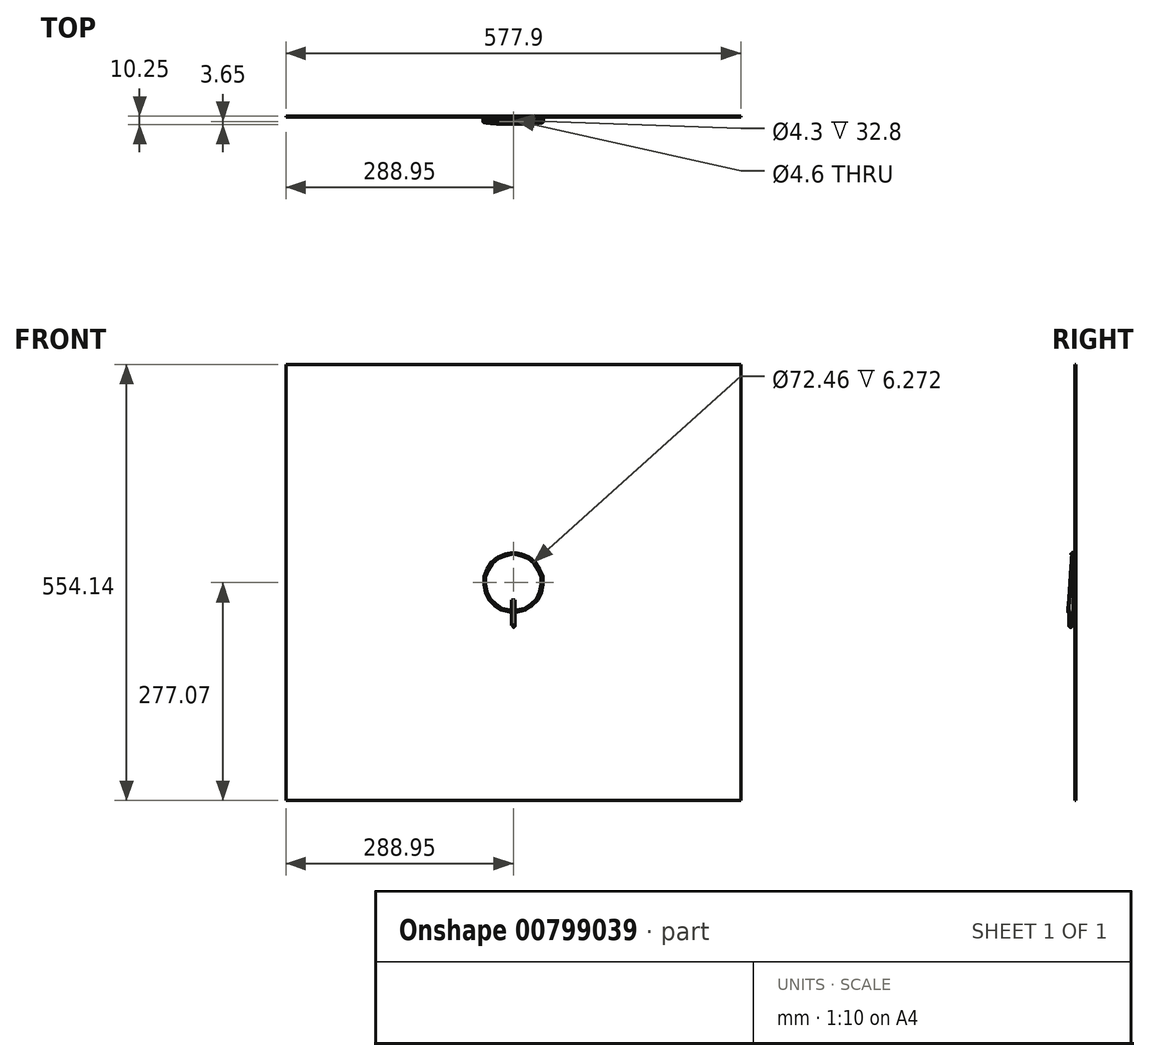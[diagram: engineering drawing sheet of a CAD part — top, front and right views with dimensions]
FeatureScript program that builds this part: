
annotation { "Feature Type Name" : "Feature", "Feature Type Description" : "" }
export const myFeature = defineFeature(function(context is Context, id is Id, definition is map)
    precondition{}
    {
        {
            var Q0;
            Q0=qCreatedBy(makeId("Front.planeOp"),FACE);
            var sketch = newSketch(context, id + "F0", { "sketchPlane" : qUnion([Q0])});
            skCircle(sketch, "E0", {"center": v(0, 0) * mm, "radius": 38.46 * mm});
            skCircle(sketch, "E1", {"center": v(0, 0) * mm, "radius": 36.23 * mm});
            skSolve(sketch);
        }
        {
            var Q0;
            Q0=makeQuery(id+"F0.imprint","IMPRINT",FACE,{"disambiguationData":[TD([[makeQuery(id+"F0.imprint","IMPRINT",EDGE,{"derivedFrom":sQuery(id+"F0.wireOp",EDGE,"E0")}),1.0]])]});
            extrude(context, id + "F1", {"entities" : qUnion([Q0]), "depth" : 8.4 * mm, "offsetDistance" : 25 * mm});
        }
        {
            var Q0;
            Q0=qCreatedBy(makeId("Right.planeOp"),FACE);
            var sketch = newSketch(context, id + "F2", { "sketchPlane" : qUnion([Q0])});
            skLineSegment(sketch, "E2", {"start": v(-21.96, 45.14) * mm, "end": v(-4.24, 45.14) * mm});
            skLineSegment(sketch, "E3", {"start": v(-4.24, 45.14) * mm, "end": v(-2, 39.27) * mm});
            skLineSegment(sketch, "E4", {"start": v(-2, 39.27) * mm, "end": v(-8, -48.33) * mm});
            skLineSegment(sketch, "E5", {"start": v(-8, -48.33) * mm, "end": v(-24.72, -40.34) * mm});
            skLineSegment(sketch, "E6", {"start": v(-24.72, -40.34) * mm, "end": v(-21.96, 45.14) * mm});
            skSolve(sketch);
        }
        {
            var Q0;
            Q0 = qSketchRegion(id + "F2", true);
            extrude(context, id + "F3", {"entities" : qUnion([Q0]), "operationType" : NewBodyOperationType.REMOVE, "endBound" : BoundingType.SYMMETRIC, "oppositeDirection" : true, "depth" : 106 * mm, "offsetDistance" : 25 * mm});
        }
        {
            var Q0;
            Q0=makeQuery(id+"F3.boolean.opBoolean","INTERSECT",EDGE,{"derivedFrom":[makeQuery(id+"F1.opExtrude","SWEPT_FACE",FACE,{"disambiguationData":[OSD([sQuery(id+"F0.wireOp",EDGE,"E1")])]}),makeQuery(id+"F3.opExtrude","SWEPT_FACE",FACE,{"disambiguationData":[OSD([sQuery(id+"F2.wireOp",EDGE,"E4")])]})]});
            var Q1;
            Q1=makeQuery(id+"F3.boolean.opBoolean","INTERSECT",EDGE,{"derivedFrom":[makeQuery(id+"F1.opExtrude","SWEPT_FACE",FACE,{"disambiguationData":[OSD([sQuery(id+"F0.wireOp",EDGE,"E0")])]}),makeQuery(id+"F3.opExtrude","SWEPT_FACE",FACE,{"disambiguationData":[OSD([sQuery(id+"F2.wireOp",EDGE,"E4")])]})]});
            fillet(context, id + "F4", {"entities" : qUnion([Q0, Q1]), "radius" : 1 * mm, "tangentPropagation" : true, "allowEdgeOverflow" : false});
        }
        {
            var Q0;
            Q0=qCreatedBy(makeId("Top.planeOp"),FACE);
            var sketch = newSketch(context, id + "F5", { "sketchPlane" : qUnion([Q0])});
            skCircle(sketch, "E7", {"center": v(0, -3.6) * mm, "radius": 2.3 * mm});
            skSolve(sketch);
        }
        {
            var Q0;
            Q0=qCreatedBy(makeId("Top.planeOp"),FACE);
            cPlane(context, id + "F6", {"entities" : qUnion([Q0]), "cplaneType" : CPlaneType.OFFSET, "offset" : 22 * mm, "oppositeDirection" : true, "width" : 150 * mm, "height" : 150 * mm});
        }
        {
            var Q0;
            Q0=qCreatedBy(id+"F6.planeOp",FACE);
            var sketch = newSketch(context, id + "F7", { "sketchPlane" : qUnion([Q0])});
            skCircle(sketch, "E8", {"center": v(0, -3.6) * mm, "radius": 2.25 * mm});
            skSolve(sketch);
        }
        {
            var Q0;
            Q0=makeQuery(id+"F5.imprint","IMPRINT",FACE,{"disambiguationData":[TD([[makeQuery(id+"F5.imprint","IMPRINT",EDGE,{"derivedFrom":sQuery(id+"F5.wireOp",EDGE,"E7")}),1.0]])]});
            extrude(context, id + "F8", {"entities" : qUnion([Q0]), "operationType" : NewBodyOperationType.REMOVE, "oppositeDirection" : true, "depth" : 45.9 * mm, "offsetDistance" : 25 * mm});
        }
        {
            var Q0;
            Q0=makeQuery(id+"F8.boolean.opBoolean","INTERSECT",EDGE,{"derivedFrom":[makeQuery(id+"F1.opExtrude","SWEPT_FACE",FACE,{"disambiguationData":[OSD([sQuery(id+"F0.wireOp",EDGE,"E1")])]}),makeQuery(id+"F8.opExtrude","SWEPT_FACE",FACE,{"disambiguationData":[OSD([sQuery(id+"F5.wireOp",EDGE,"E7")])]})]});
            var Q1;
            Q1=makeQuery(id+"F8.boolean.opBoolean","INTERSECT",EDGE,{"derivedFrom":[makeQuery(id+"F1.opExtrude","SWEPT_FACE",FACE,{"disambiguationData":[OSD([sQuery(id+"F0.wireOp",EDGE,"E0")])]}),makeQuery(id+"F8.opExtrude","SWEPT_FACE",FACE,{"disambiguationData":[OSD([sQuery(id+"F5.wireOp",EDGE,"E7")])]})]});
            fillet(context, id + "F9", {"entities" : qUnion([Q0, Q1]), "radius" : 0.3 * mm, "tangentPropagation" : true, "allowEdgeOverflow" : false});
        }
        {
            var Q0;
            Q0 = qSketchRegion(id + "F7", true);
            extrude(context, id + "F10", {"entities" : qUnion([Q0]), "operationType" : NewBodyOperationType.ADD, "oppositeDirection" : true, "depth" : 35 * mm, "offsetDistance" : 25 * mm});
        }
        {
            var Q0;
            Q0=makeQuery(id+"F10.opExtrude","CAP_EDGE",EDGE,{"disambiguationData":[OSD([sQuery(id+"F7.wireOp",EDGE,"E8")])],"isStart":false});
            fillet(context, id + "F11", {"entities" : qUnion([Q0]), "radius" : 2.2 * mm, "tangentPropagation" : true, "allowEdgeOverflow" : false});
        }
        {
            var Q0;
            Q0=makeQuery(id+"F10.opExtrude","CAP_FACE",FACE,{"disambiguationData":[OSD([sQuery(id+"F7.wireOp",EDGE,"E8")])],"isStart":true});
            shell(context, id + "F12", {"entities" : qUnion([Q0]), "thickness" : 0.1 * mm});
        }
        {
            var Q0;
            Q0=qCreatedBy(makeId("Right.planeOp"),FACE);
            var sketch = newSketch(context, id + "F13", { "sketchPlane" : qUnion([Q0])});
            skLineSegment(sketch, "E9", {"start": v(2, 35.83) * mm, "end": v(-1.89, 35.83) * mm});
            skLineSegment(sketch, "E10", {"start": v(-1.89, 35.83) * mm, "end": v(-3.62, 36.57) * mm});
            skSolve(sketch);
        }
        {
            var Q0;
            Q0=qCreatedBy(makeId("Front.planeOp"),FACE);
            cPlane(context, id + "F14", {"entities" : qUnion([Q0]), "cplaneType" : CPlaneType.OFFSET, "offset" : 2 * mm, "oppositeDirection" : true, "width" : 150 * mm, "height" : 150 * mm});
        }
        {
            var Q0;
            Q0=qCreatedBy(id+"F14.planeOp",FACE);
            var sketch = newSketch(context, id + "F15", { "sketchPlane" : qUnion([Q0])});
            skCircle(sketch, "E11", {"center": v(0, 35.84) * mm, "radius": 0.35 * mm});
            skSolve(sketch);
        }
        {
            var Q0;
            Q0=makeQuery(id+"F15.imprint","IMPRINT",FACE,{"disambiguationData":[TD([[makeQuery(id+"F15.imprint","IMPRINT",EDGE,{"derivedFrom":sQuery(id+"F15.wireOp",EDGE,"E11")}),1.0]])]});
            var Q1;
            Q1=sQuery(id+"F13.wireOp",EDGE,"E9");
            var Q2;
            Q2=sQuery(id+"F13.wireOp",EDGE,"E10");
            sweep(context, id + "F16", {"profiles" : qUnion([Q0]), "path" : qUnion([Q1, Q2])});
        }
        {
            var Q0;
            Q0=makeQuery(id+"F16.opSweep","CAP_EDGE",EDGE,{"disambiguationData":[OSD([sQuery(id+"F13.wireOp",VERTEX,"E10.end"),sQuery(id+"F15.wireOp",EDGE,"E11")])],"isStart":false});
            fillet(context, id + "F17", {"entities" : qUnion([Q0]), "radius" : 0.3 * mm, "tangentPropagation" : true, "allowEdgeOverflow" : false});
        }
        {
            var Q0;
            Q0=qCreatedBy(id+"F14.planeOp",FACE);
            var sketch = newSketch(context, id + "F18", { "sketchPlane" : qUnion([Q0])});
            skLineSegment(sketch, "E12.bottom", {"start": v(288.95, 277.07) * mm, "end": v(-288.95, 277.07) * mm});
            skLineSegment(sketch, "E12.top", {"start": v(288.95, -277.07) * mm, "end": v(-288.95, -277.07) * mm});
            skLineSegment(sketch, "E12.left", {"start": v(288.95, 277.07) * mm, "end": v(288.95, -277.07) * mm});
            skLineSegment(sketch, "E12.right", {"start": v(-288.95, 277.07) * mm, "end": v(-288.95, -277.07) * mm});
            skPoint(sketch, "E12.middle", {"position": v(0, 0) * mm});
            skSolve(sketch);
        }
        {
            var Q0;
            Q0 = qSketchRegion(id + "F18", true);
            extrude(context, id + "F19", {"entities" : qUnion([Q0]), "operationType" : NewBodyOperationType.ADD, "oppositeDirection" : true, "depth" : 1 * mm, "offsetDistance" : 25 * mm});
        }
    });
